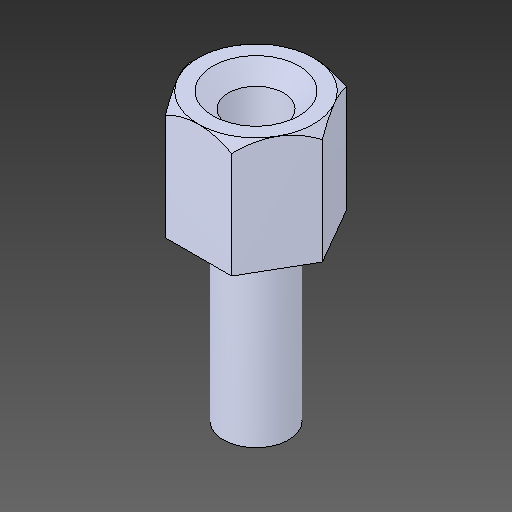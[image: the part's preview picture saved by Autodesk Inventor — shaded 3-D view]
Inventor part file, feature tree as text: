
AUTODESK INVENTOR PART (.ipt)
format: ipt  version: 2018.2 (Build 222227000, 227)  size: 111,104 bytes
history: native  units: mm
features: other x1, chamfer x1
ambient origin geometry x8: Origin, YZ Plane, XZ Plane, XY Plane, X Axis, Y Axis, Z Axis, Center Point
bodies: Body1 (feature_tree)
feature tree (2):
  other  "ソリッド1"
  chamfer  "Chamfer1"  [1 undecoded]
note: 1 required parameter value undecoded (feature->parameter linkage not recoverable at this tier; creation-order binding heuristic only, values carry confidence <= 0.55)
